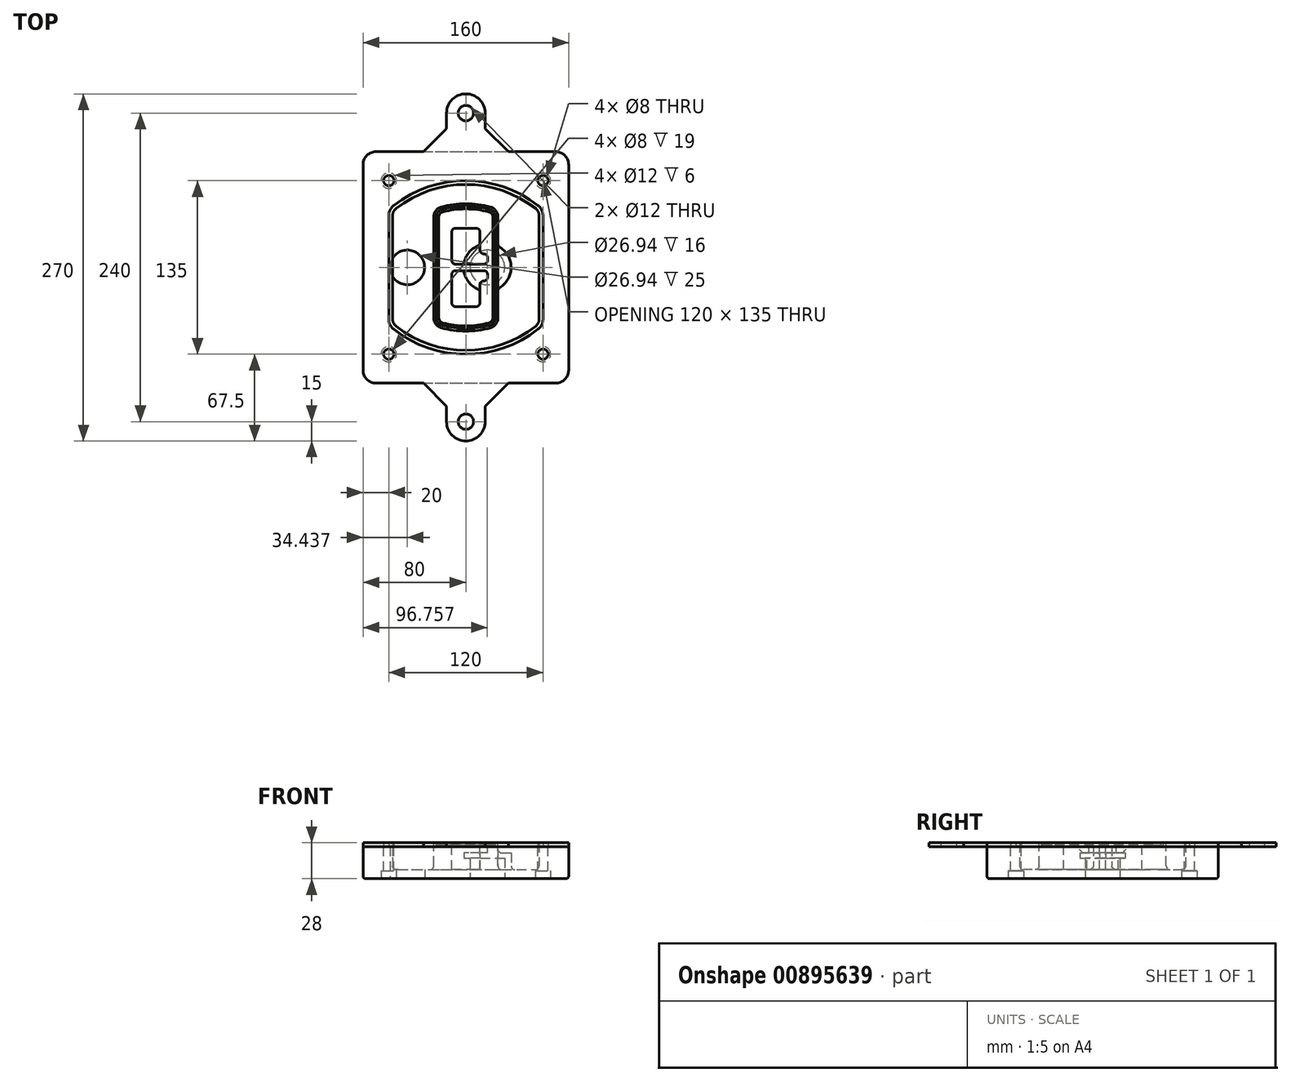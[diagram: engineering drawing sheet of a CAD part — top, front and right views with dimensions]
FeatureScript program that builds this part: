
annotation { "Feature Type Name" : "Feature", "Feature Type Description" : "" }
export const myFeature = defineFeature(function(context is Context, id is Id, definition is map)
    precondition{}
    {
        {
            var Q0;
            Q0=qCreatedBy(makeId("Top.planeOp"),FACE);
            var sketch = newSketch(context, id + "F0", { "sketchPlane" : qUnion([Q0])});
            skPoint(sketch, "E0.rect.middle", {"position": v(0, 0) * mm});
            skLineSegment(sketch, "E1.bottom", {"start": v(-70, -90) * mm, "end": v(70, -90) * mm});
            skLineSegment(sketch, "E1.top", {"start": v(-70, 90) * mm, "end": v(70, 90) * mm});
            skLineSegment(sketch, "E1.left", {"start": v(-80, -80) * mm, "end": v(-80, 80) * mm});
            skLineSegment(sketch, "E1.right", {"start": v(80, -80) * mm, "end": v(80, 80) * mm});
            skLineSegment(sketch, "E2", {"start": v(-80, 90) * mm, "end": v(80, -90) * mm, "construction": true});
            skLineSegment(sketch, "E3", {"start": v(80, 90) * mm, "end": v(-80, -90) * mm, "construction": true});
            skCircle(sketch, "E4", {"center": v(-60, 67.5) * mm, "radius": 4 * mm});
            skCircle(sketch, "E5", {"center": v(60, 67.5) * mm, "radius": 4 * mm});
            skCircle(sketch, "E6", {"center": v(60, -67.5) * mm, "radius": 4 * mm});
            skCircle(sketch, "E7", {"center": v(-60, -67.5) * mm, "radius": 4 * mm});
            skLineSegment(sketch, "E8", {"start": v(-60, 67.5) * mm, "end": v(60, 67.5) * mm, "construction": true});
            skLineSegment(sketch, "E9", {"start": v(60, 67.5) * mm, "end": v(60, -67.5) * mm, "construction": true});
            skLineSegment(sketch, "E10", {"start": v(60, -67.5) * mm, "end": v(-60, -67.5) * mm, "construction": true});
            skLineSegment(sketch, "E11", {"start": v(-60, -67.5) * mm, "end": v(-60, 67.5) * mm, "construction": true});
            skLineSegment(sketch, "E12", {"start": v(-60, 40.3) * mm, "end": v(-60, -40.3) * mm});
            skLineSegment(sketch, "E13", {"start": v(60, 40.3) * mm, "end": v(60, -40.3) * mm});
            skArc(sketch, "E14", {"start": v(56.15, 48.18) * mm, "mid": v(0, 67.5) * mm, "end": v(-56.15, 48.18) * mm});
            skArc(sketch, "E15", {"start": v(-56.15, -48.18) * mm, "mid": v(0, -67.5) * mm, "end": v(56.15, -48.18) * mm});
            skLineSegment(sketch, "E16", {"start": v(-60, 0) * mm, "end": v(60, 0) * mm, "construction": true});
            skPoint(sketch, "E17.visualSharp", {"position": v(-60, -45) * mm});
            skArc(sketch, "E17.filletArc", {"start": v(-60, -40.3) * mm, "mid": v(-58.99, -44.68) * mm, "end": v(-56.15, -48.18) * mm});
            skPoint(sketch, "E18.visualSharp", {"position": v(-60, 45) * mm});
            skArc(sketch, "E18.filletArc", {"start": v(-56.15, 48.18) * mm, "mid": v(-58.99, 44.68) * mm, "end": v(-60, 40.3) * mm});
            skPoint(sketch, "E19.visualSharp", {"position": v(60, 45) * mm});
            skArc(sketch, "E19.filletArc", {"start": v(60, 40.3) * mm, "mid": v(58.99, 44.68) * mm, "end": v(56.15, 48.18) * mm});
            skPoint(sketch, "E20.visualSharp", {"position": v(60, -45) * mm});
            skArc(sketch, "E20.filletArc", {"start": v(56.15, -48.18) * mm, "mid": v(58.99, -44.68) * mm, "end": v(60, -40.3) * mm});
            skPoint(sketch, "E21.visualSharp", {"position": v(-80, 90) * mm});
            skArc(sketch, "E21.filletArc", {"start": v(-70, 90) * mm, "mid": v(-77.07, 87.07) * mm, "end": v(-80, 80) * mm});
            skPoint(sketch, "E22.visualSharp", {"position": v(80, 90) * mm});
            skArc(sketch, "E22.filletArc", {"start": v(80, 80) * mm, "mid": v(77.07, 87.07) * mm, "end": v(70, 90) * mm});
            skPoint(sketch, "E23.visualSharp", {"position": v(80, -90) * mm});
            skArc(sketch, "E23.filletArc", {"start": v(70, -90) * mm, "mid": v(77.07, -87.07) * mm, "end": v(80, -80) * mm});
            skPoint(sketch, "E24.visualSharp", {"position": v(-80, -90) * mm});
            skArc(sketch, "E24.filletArc", {"start": v(-80, -80) * mm, "mid": v(-77.07, -87.07) * mm, "end": v(-70, -90) * mm});
            skArc(sketch, "E25.0", {"start": v(57, 40.3) * mm, "mid": v(56.3, 43.36) * mm, "end": v(54.3, 45.81) * mm});
            skLineSegment(sketch, "E25.1", {"start": v(57, 40.3) * mm, "end": v(57, -40.3) * mm});
            skArc(sketch, "E25.2", {"start": v(54.3, -45.81) * mm, "mid": v(56.3, -43.36) * mm, "end": v(57, -40.3) * mm});
            skArc(sketch, "E25.3", {"start": v(-54.3, -45.81) * mm, "mid": v(0, -64.5) * mm, "end": v(54.3, -45.81) * mm});
            skArc(sketch, "E25.4", {"start": v(-57, -40.3) * mm, "mid": v(-56.3, -43.36) * mm, "end": v(-54.3, -45.81) * mm});
            skArc(sketch, "E25.5", {"start": v(54.3, 45.81) * mm, "mid": v(0, 64.5) * mm, "end": v(-54.3, 45.81) * mm});
            skLineSegment(sketch, "E25.6", {"start": v(-57, 40.3) * mm, "end": v(-57, -40.3) * mm});
            skArc(sketch, "E25.7", {"start": v(-54.3, 45.81) * mm, "mid": v(-56.3, 43.36) * mm, "end": v(-57, 40.3) * mm});
            skArc(sketch, "E26.0", {"start": v(-58.62, 51.33) * mm, "mid": v(-62.58, 46.43) * mm, "end": v(-64, 40.3) * mm});
            skArc(sketch, "E26.1", {"start": v(58.62, 51.33) * mm, "mid": v(0, 71.5) * mm, "end": v(-58.62, 51.33) * mm});
            skArc(sketch, "E26.2", {"start": v(64, 40.3) * mm, "mid": v(62.58, 46.43) * mm, "end": v(58.62, 51.33) * mm});
            skLineSegment(sketch, "E26.3", {"start": v(64, 40.3) * mm, "end": v(64, -40.3) * mm});
            skArc(sketch, "E26.4", {"start": v(58.62, -51.33) * mm, "mid": v(62.58, -46.43) * mm, "end": v(64, -40.3) * mm});
            skLineSegment(sketch, "E26.5", {"start": v(-64, 40.3) * mm, "end": v(-64, -40.3) * mm});
            skArc(sketch, "E26.6", {"start": v(-58.62, -51.33) * mm, "mid": v(0, -71.5) * mm, "end": v(58.62, -51.33) * mm});
            skArc(sketch, "E26.7", {"start": v(-64, -40.3) * mm, "mid": v(-62.58, -46.43) * mm, "end": v(-58.62, -51.33) * mm});
            skSolve(sketch);
        }
        {
            var Q0;
            Q0=makeQuery(id+"F0.imprint","IMPRINT",FACE,{"disambiguationData":[TD([[makeQuery(id+"F0.imprint","IMPRINT",EDGE,{"derivedFrom":sQuery(id+"F0.wireOp",EDGE,"E1.bottom")}),1.0]])]});
            var Q1;
            Q1=makeQuery(id+"F0.imprint","IMPRINT",FACE,{"disambiguationData":[TD([[makeQuery(id+"F0.imprint","IMPRINT",EDGE,{"derivedFrom":sQuery(id+"F0.wireOp",EDGE,"E12")}),1.0]])]});
            var Q2;
            Q2=makeQuery(id+"F0.imprint","IMPRINT",FACE,{"disambiguationData":[TD([[makeQuery(id+"F0.imprint","IMPRINT",EDGE,{"derivedFrom":sQuery(id+"F0.wireOp",EDGE,"E25.0")}),1.0]])]});
            var Q3;
            Q3=makeQuery(id+"F0.imprint","IMPRINT",FACE,{"disambiguationData":[TD([[makeQuery(id+"F0.imprint","IMPRINT",EDGE,{"derivedFrom":sQuery(id+"F0.wireOp",EDGE,"E12")}),-1.0]])]});
            extrude(context, id + "F1", {"entities" : qUnion([Q0, Q1, Q2, Q3]), "oppositeDirection" : true, "depth" : 25 * mm});
        }
        {
            var Q0;
            Q0=makeQuery(id+"F0.imprint","IMPRINT",FACE,{"disambiguationData":[TD([[makeQuery(id+"F0.imprint","IMPRINT",EDGE,{"derivedFrom":sQuery(id+"F0.wireOp",EDGE,"E12")}),1.0]])]});
            extrude(context, id + "F2", {"entities" : qUnion([Q0]), "operationType" : NewBodyOperationType.ADD, "depth" : 3 * mm});
        }
        {
            var Q0;
            Q0=makeQuery(id+"F0.imprint","IMPRINT",FACE,{"disambiguationData":[TD([[makeQuery(id+"F0.imprint","IMPRINT",EDGE,{"derivedFrom":sQuery(id+"F0.wireOp",EDGE,"E25.0")}),1.0]])]});
            extrude(context, id + "F3", {"entities" : qUnion([Q0]), "operationType" : NewBodyOperationType.REMOVE, "oppositeDirection" : true, "depth" : 18 * mm});
        }
        {
            var Q0;
            Q0=makeQuery(id+"F2.opExtrude","CAP_FACE",FACE,{"disambiguationData":[OSD([sQuery(id+"F0.wireOp",EDGE,"E12"),sQuery(id+"F0.wireOp",EDGE,"E13"),sQuery(id+"F0.wireOp",EDGE,"E14"),sQuery(id+"F0.wireOp",EDGE,"E15"),sQuery(id+"F0.wireOp",EDGE,"E17.filletArc"),sQuery(id+"F0.wireOp",EDGE,"E18.filletArc"),sQuery(id+"F0.wireOp",EDGE,"E19.filletArc"),sQuery(id+"F0.wireOp",EDGE,"E20.filletArc"),sQuery(id+"F0.wireOp",EDGE,"E25.0"),sQuery(id+"F0.wireOp",EDGE,"E25.1"),sQuery(id+"F0.wireOp",EDGE,"E25.2"),sQuery(id+"F0.wireOp",EDGE,"E25.3"),sQuery(id+"F0.wireOp",EDGE,"E25.4"),sQuery(id+"F0.wireOp",EDGE,"E25.5"),sQuery(id+"F0.wireOp",EDGE,"E25.6"),sQuery(id+"F0.wireOp",EDGE,"E25.7")])],"isStart":false});
            var sketch = newSketch(context, id + "F4", { "sketchPlane" : qUnion([Q0])});
            skArc(sketch, "E27.0", {"start": v(-19.08, -46.97) * mm, "mid": v(0, -49.5) * mm, "end": v(19.08, -46.97) * mm});
            skArc(sketch, "E28.0", {"start": v(19.08, 46.97) * mm, "mid": v(0, 49.5) * mm, "end": v(-19.08, 46.97) * mm});
            skLineSegment(sketch, "E29", {"start": v(-25, 39.25) * mm, "end": v(-25, -39.25) * mm});
            skLineSegment(sketch, "E30", {"start": v(25, 39.25) * mm, "end": v(25, -39.25) * mm});
            skLineSegment(sketch, "E31", {"start": v(-25, 45.1) * mm, "end": v(25, 45.1) * mm, "construction": true});
            skLineSegment(sketch, "E32", {"start": v(-25, -45.1) * mm, "end": v(25, -45.1) * mm, "construction": true});
            skPoint(sketch, "E33.visualSharp", {"position": v(-25, 45.1) * mm});
            skArc(sketch, "E33.filletArc", {"start": v(-19.08, 46.97) * mm, "mid": v(-23.35, 44.11) * mm, "end": v(-25, 39.25) * mm});
            skPoint(sketch, "E34.visualSharp", {"position": v(25, 45.1) * mm});
            skArc(sketch, "E34.filletArc", {"start": v(25, 39.25) * mm, "mid": v(23.35, 44.11) * mm, "end": v(19.08, 46.97) * mm});
            skPoint(sketch, "E35.visualSharp", {"position": v(25, -45.1) * mm});
            skArc(sketch, "E35.filletArc", {"start": v(19.08, -46.97) * mm, "mid": v(23.35, -44.11) * mm, "end": v(25, -39.25) * mm});
            skPoint(sketch, "E36.visualSharp", {"position": v(-25, -45.1) * mm});
            skArc(sketch, "E36.filletArc", {"start": v(-25, -39.25) * mm, "mid": v(-23.35, -44.11) * mm, "end": v(-19.08, -46.97) * mm});
            skArc(sketch, "E37.0", {"start": v(54.3, 45.81) * mm, "mid": v(0, 64.5) * mm, "end": v(-54.3, 45.81) * mm});
            skArc(sketch, "E37.1", {"start": v(-54.3, 45.81) * mm, "mid": v(-56.3, 43.36) * mm, "end": v(-57, 40.3) * mm});
            skLineSegment(sketch, "E37.2", {"start": v(-57, 40.3) * mm, "end": v(-57, -40.3) * mm});
            skArc(sketch, "E37.3", {"start": v(-57, -40.3) * mm, "mid": v(-56.3, -43.36) * mm, "end": v(-54.3, -45.81) * mm});
            skArc(sketch, "E37.4", {"start": v(-54.3, -45.81) * mm, "mid": v(0, -64.5) * mm, "end": v(54.3, -45.81) * mm});
            skArc(sketch, "E37.5", {"start": v(54.3, -45.81) * mm, "mid": v(56.3, -43.36) * mm, "end": v(57, -40.3) * mm});
            skLineSegment(sketch, "E37.6", {"start": v(57, 40.3) * mm, "end": v(57, -40.3) * mm});
            skArc(sketch, "E37.7", {"start": v(57, 40.3) * mm, "mid": v(56.3, 43.36) * mm, "end": v(54.3, 45.81) * mm});
            skLineSegment(sketch, "E38.0", {"start": v(23, 39.25) * mm, "end": v(23, -39.25) * mm});
            skArc(sketch, "E38.1", {"start": v(18.56, -45.04) * mm, "mid": v(21.76, -42.9) * mm, "end": v(23, -39.25) * mm});
            skArc(sketch, "E38.2", {"start": v(-18.56, -45.04) * mm, "mid": v(0, -47.5) * mm, "end": v(18.56, -45.04) * mm});
            skArc(sketch, "E38.3", {"start": v(-23, -39.25) * mm, "mid": v(-21.76, -42.9) * mm, "end": v(-18.56, -45.04) * mm});
            skLineSegment(sketch, "E38.4", {"start": v(-23, 39.25) * mm, "end": v(-23, -39.25) * mm});
            skArc(sketch, "E38.5", {"start": v(23, 39.25) * mm, "mid": v(21.76, 42.9) * mm, "end": v(18.56, 45.04) * mm});
            skArc(sketch, "E38.6", {"start": v(-18.56, 45.04) * mm, "mid": v(-21.76, 42.9) * mm, "end": v(-23, 39.25) * mm});
            skArc(sketch, "E38.7", {"start": v(18.56, 45.04) * mm, "mid": v(0, 47.5) * mm, "end": v(-18.56, 45.04) * mm});
            skArc(sketch, "E39.0", {"start": v(21, 39.25) * mm, "mid": v(20.18, 41.68) * mm, "end": v(18.04, 43.1) * mm});
            skLineSegment(sketch, "E39.1", {"start": v(21, 39.25) * mm, "end": v(21, -39.25) * mm});
            skArc(sketch, "E39.2", {"start": v(18.04, -43.1) * mm, "mid": v(20.18, -41.68) * mm, "end": v(21, -39.25) * mm});
            skArc(sketch, "E39.3", {"start": v(-18.04, -43.1) * mm, "mid": v(0, -45.5) * mm, "end": v(18.04, -43.1) * mm});
            skArc(sketch, "E39.4", {"start": v(-21, -39.25) * mm, "mid": v(-20.18, -41.68) * mm, "end": v(-18.04, -43.1) * mm});
            skArc(sketch, "E39.5", {"start": v(18.04, 43.1) * mm, "mid": v(0, 45.5) * mm, "end": v(-18.04, 43.1) * mm});
            skLineSegment(sketch, "E39.6", {"start": v(-21, 39.25) * mm, "end": v(-21, -39.25) * mm});
            skArc(sketch, "E39.7", {"start": v(-18.04, 43.1) * mm, "mid": v(-20.18, 41.68) * mm, "end": v(-21, 39.25) * mm});
            skLineSegment(sketch, "E40", {"start": v(-25, 0) * mm, "end": v(25, 0) * mm, "construction": true});
            skLineSegment(sketch, "E41", {"start": v(-11, 5.5) * mm, "end": v(-11, 27.5) * mm});
            skLineSegment(sketch, "E42", {"start": v(-8, 30.5) * mm, "end": v(8, 30.5) * mm});
            skLineSegment(sketch, "E43", {"start": v(11, 27.5) * mm, "end": v(11, 13.5) * mm});
            skLineSegment(sketch, "E44", {"start": v(14, 10.5) * mm, "end": v(14, 10.5) * mm});
            skLineSegment(sketch, "E45", {"start": v(17, 7.5) * mm, "end": v(17, 5.5) * mm});
            skLineSegment(sketch, "E46", {"start": v(14, 2.5) * mm, "end": v(-8, 2.5) * mm});
            skPoint(sketch, "E47.visualSharp", {"position": v(-11, 30.5) * mm});
            skArc(sketch, "E47.filletArc", {"start": v(-8, 30.5) * mm, "mid": v(-10.12, 29.62) * mm, "end": v(-11, 27.5) * mm});
            skPoint(sketch, "E48.visualSharp", {"position": v(11, 30.5) * mm});
            skArc(sketch, "E48.filletArc", {"start": v(11, 27.5) * mm, "mid": v(10.12, 29.62) * mm, "end": v(8, 30.5) * mm});
            skPoint(sketch, "E49.visualSharp", {"position": v(11, 10.5) * mm});
            skArc(sketch, "E49.filletArc", {"start": v(11, 13.5) * mm, "mid": v(11.88, 11.38) * mm, "end": v(14, 10.5) * mm});
            skPoint(sketch, "E50.visualSharp", {"position": v(17, 10.5) * mm});
            skArc(sketch, "E50.filletArc", {"start": v(17, 7.5) * mm, "mid": v(16.12, 9.62) * mm, "end": v(14, 10.5) * mm});
            skPoint(sketch, "E51.visualSharp", {"position": v(17, 2.5) * mm});
            skArc(sketch, "E51.filletArc", {"start": v(14, 2.5) * mm, "mid": v(16.12, 3.38) * mm, "end": v(17, 5.5) * mm});
            skPoint(sketch, "E52.visualSharp", {"position": v(-11, 2.5) * mm});
            skArc(sketch, "E52.filletArc", {"start": v(-11, 5.5) * mm, "mid": v(-10.12, 3.38) * mm, "end": v(-8, 2.5) * mm});
            skLineSegment(sketch, "E53.0.MirrorCS", {"start": v(14, -2.5) * mm, "end": v(-8, -2.5) * mm});
            skArc(sketch, "E54.0.MirrorCS", {"start": v(-11, -5.5) * mm, "mid": v(-10.12, -3.38) * mm, "end": v(-8, -2.5) * mm});
            skLineSegment(sketch, "E55.0.MirrorCS", {"start": v(-11, -5.5) * mm, "end": v(-11, -27.5) * mm});
            skArc(sketch, "E56.0.MirrorCS", {"start": v(-8, -30.5) * mm, "mid": v(-10.12, -29.62) * mm, "end": v(-11, -27.5) * mm});
            skLineSegment(sketch, "E57.0.MirrorCS", {"start": v(-8, -30.5) * mm, "end": v(8, -30.5) * mm});
            skArc(sketch, "E58.0.MirrorCS", {"start": v(11, -27.5) * mm, "mid": v(10.12, -29.62) * mm, "end": v(8, -30.5) * mm});
            skLineSegment(sketch, "E59.0.MirrorCS", {"start": v(11, -27.5) * mm, "end": v(11, -13.5) * mm});
            skArc(sketch, "E60.0.MirrorCS", {"start": v(11, -13.5) * mm, "mid": v(11.88, -11.38) * mm, "end": v(14, -10.5) * mm});
            skArc(sketch, "E61.0.MirrorCS", {"start": v(17, -7.5) * mm, "mid": v(16.12, -9.62) * mm, "end": v(14, -10.5) * mm});
            skLineSegment(sketch, "E62.0.MirrorCS", {"start": v(17, -7.5) * mm, "end": v(17, -5.5) * mm});
            skArc(sketch, "E63.0.MirrorCS", {"start": v(14, -2.5) * mm, "mid": v(16.12, -3.38) * mm, "end": v(17, -5.5) * mm});
            skSolve(sketch);
        }
        {
            var Q0;
            Q0=makeQuery(id+"F4.imprint","IMPRINT",FACE,{"disambiguationData":[TD([[makeQuery(id+"F4.imprint","IMPRINT",EDGE,{"derivedFrom":sQuery(id+"F4.wireOp",EDGE,"E27.0")}),1.0]])]});
            var Q1;
            Q1=makeQuery(id+"F4.imprint","IMPRINT",FACE,{"disambiguationData":[TD([[makeQuery(id+"F4.imprint","IMPRINT",EDGE,{"derivedFrom":sQuery(id+"F4.wireOp",EDGE,"E38.0")}),-1.0]])]});
            var Q2;
            Q2=makeQuery(id+"F4.imprint","IMPRINT",FACE,{"disambiguationData":[TD([[makeQuery(id+"F4.imprint","IMPRINT",EDGE,{"derivedFrom":sQuery(id+"F4.wireOp",EDGE,"E39.0")}),1.0]])]});
            extrude(context, id + "F5", {"entities" : qUnion([Q0, Q1, Q2]), "operationType" : NewBodyOperationType.ADD, "endBound" : BoundingType.UP_TO_NEXT, "oppositeDirection" : true, "depth" : 25 * mm});
        }
        {
            var Q0;
            Q0=makeQuery(id+"F4.imprint","IMPRINT",FACE,{"disambiguationData":[TD([[makeQuery(id+"F4.imprint","IMPRINT",EDGE,{"derivedFrom":sQuery(id+"F4.wireOp",EDGE,"E38.0")}),-1.0]])]});
            extrude(context, id + "F6", {"entities" : qUnion([Q0]), "operationType" : NewBodyOperationType.REMOVE, "oppositeDirection" : true, "depth" : 2 * mm});
        }
        {
            var Q0;
            Q0=makeQuery(id+"F1.opExtrude","CAP_FACE",FACE,{"disambiguationData":[OSD([sQuery(id+"F0.wireOp",EDGE,"E1.bottom"),sQuery(id+"F0.wireOp",EDGE,"E1.top"),sQuery(id+"F0.wireOp",EDGE,"E1.left"),sQuery(id+"F0.wireOp",EDGE,"E1.right"),sQuery(id+"F0.wireOp",EDGE,"E4"),sQuery(id+"F0.wireOp",EDGE,"E5"),sQuery(id+"F0.wireOp",EDGE,"E6"),sQuery(id+"F0.wireOp",EDGE,"E7"),sQuery(id+"F0.wireOp",EDGE,"E21.filletArc"),sQuery(id+"F0.wireOp",EDGE,"E22.filletArc"),sQuery(id+"F0.wireOp",EDGE,"E23.filletArc"),sQuery(id+"F0.wireOp",EDGE,"E24.filletArc")])],"isStart":false});
            var sketch = newSketch(context, id + "F7", { "sketchPlane" : qUnion([Q0])});
            skCircle(sketch, "E64", {"center": v(16.76, 0) * mm, "radius": 13.47 * mm});
            skCircle(sketch, "E65", {"center": v(-45.56, 0) * mm, "radius": 13.47 * mm});
            skLineSegment(sketch, "E66", {"start": v(80, 0) * mm, "end": v(-80, 0) * mm});
            skCircle(sketch, "E67", {"center": v(16.76, 0) * mm, "radius": 18.47 * mm});
            skCircle(sketch, "E68", {"center": v(60, -67.5) * mm, "radius": 6 * mm});
            skCircle(sketch, "E69", {"center": v(-60, -67.5) * mm, "radius": 6 * mm});
            skCircle(sketch, "E70", {"center": v(-60, 67.5) * mm, "radius": 6 * mm});
            skCircle(sketch, "E71", {"center": v(60, 67.5) * mm, "radius": 6 * mm});
            skSolve(sketch);
        }
        {
            var Q0;
            {var subQ1=sQuery(id+"F7.wireOp",EDGE,"E66");var subQ4=sQuery(id+"F7.wireOp",EDGE,"E64");var subQ6=makeQuery(id+"F7.imprint","INTERSECT",VERTEX,{"disambiguationData":[OD(0.0)],"derivedFrom":[subQ4,subQ1]});Q0=makeQuery(id+"F7.imprint","IMPRINT",FACE,{"disambiguationData":[TD([[makeQuery(id+"F7.imprint","IMPRINT",EDGE,{"disambiguationData":[TD([[subQ6,-1.0]])],"derivedFrom":subQ4}),-1.0]])]});}
            var Q1;
            {var subQ0=sQuery(id+"F7.wireOp",EDGE,"E66");var subQ1=sQuery(id+"F7.wireOp",EDGE,"E64");var subQ3=makeQuery(id+"F7.imprint","INTERSECT",VERTEX,{"disambiguationData":[OD(0.0)],"derivedFrom":[subQ1,subQ0]});Q1=makeQuery(id+"F7.imprint","IMPRINT",FACE,{"disambiguationData":[TD([[makeQuery(id+"F7.imprint","IMPRINT",EDGE,{"disambiguationData":[TD([[subQ3,-1.0]])],"derivedFrom":subQ1}),1.0]])]});}
            var Q2;
            {var subQ0=sQuery(id+"F7.wireOp",EDGE,"E66");var subQ1=sQuery(id+"F7.wireOp",EDGE,"E64");var subQ3=makeQuery(id+"F7.imprint","INTERSECT",VERTEX,{"disambiguationData":[OD(0.0)],"derivedFrom":[subQ1,subQ0]});Q2=makeQuery(id+"F7.imprint","IMPRINT",FACE,{"disambiguationData":[TD([[makeQuery(id+"F7.imprint","IMPRINT",EDGE,{"disambiguationData":[TD([[subQ3,1.0]])],"derivedFrom":subQ1}),1.0]])]});}
            var Q3;
            {var subQ1=sQuery(id+"F7.wireOp",EDGE,"E66");var subQ4=sQuery(id+"F7.wireOp",EDGE,"E64");var subQ6=makeQuery(id+"F7.imprint","INTERSECT",VERTEX,{"disambiguationData":[OD(0.0)],"derivedFrom":[subQ4,subQ1]});Q3=makeQuery(id+"F7.imprint","IMPRINT",FACE,{"disambiguationData":[TD([[makeQuery(id+"F7.imprint","IMPRINT",EDGE,{"disambiguationData":[TD([[subQ6,1.0]])],"derivedFrom":subQ4}),-1.0]])]});}
            extrude(context, id + "F8", {"entities" : qUnion([Q0, Q1, Q2, Q3]), "operationType" : NewBodyOperationType.ADD, "oppositeDirection" : true, "depth" : 20 * mm});
        }
        {
            var Q0;
            {var subQ0=sQuery(id+"F7.wireOp",EDGE,"E66");var subQ1=sQuery(id+"F7.wireOp",EDGE,"E64");var subQ3=makeQuery(id+"F7.imprint","INTERSECT",VERTEX,{"disambiguationData":[OD(0.0)],"derivedFrom":[subQ1,subQ0]});Q0=makeQuery(id+"F7.imprint","IMPRINT",FACE,{"disambiguationData":[TD([[makeQuery(id+"F7.imprint","IMPRINT",EDGE,{"disambiguationData":[TD([[subQ3,-1.0]])],"derivedFrom":subQ1}),1.0]])]});}
            var Q1;
            {var subQ0=sQuery(id+"F7.wireOp",EDGE,"E66");var subQ1=sQuery(id+"F7.wireOp",EDGE,"E64");var subQ3=makeQuery(id+"F7.imprint","INTERSECT",VERTEX,{"disambiguationData":[OD(0.0)],"derivedFrom":[subQ1,subQ0]});Q1=makeQuery(id+"F7.imprint","IMPRINT",FACE,{"disambiguationData":[TD([[makeQuery(id+"F7.imprint","IMPRINT",EDGE,{"disambiguationData":[TD([[subQ3,1.0]])],"derivedFrom":subQ1}),1.0]])]});}
            extrude(context, id + "F9", {"entities" : qUnion([Q0, Q1]), "operationType" : NewBodyOperationType.REMOVE, "oppositeDirection" : true, "depth" : 16 * mm});
        }
        {
            var Q0;
            {var subQ0=sQuery(id+"F7.wireOp",EDGE,"E66");var subQ1=sQuery(id+"F7.wireOp",EDGE,"E65");var subQ3=makeQuery(id+"F7.imprint","INTERSECT",VERTEX,{"disambiguationData":[OD(0.0)],"derivedFrom":[subQ1,subQ0]});Q0=makeQuery(id+"F7.imprint","IMPRINT",FACE,{"disambiguationData":[TD([[makeQuery(id+"F7.imprint","IMPRINT",EDGE,{"disambiguationData":[TD([[subQ3,-1.0]])],"derivedFrom":subQ1}),1.0]])]});}
            var Q1;
            {var subQ0=sQuery(id+"F7.wireOp",EDGE,"E66");var subQ1=sQuery(id+"F7.wireOp",EDGE,"E65");var subQ3=makeQuery(id+"F7.imprint","INTERSECT",VERTEX,{"disambiguationData":[OD(0.0)],"derivedFrom":[subQ1,subQ0]});Q1=makeQuery(id+"F7.imprint","IMPRINT",FACE,{"disambiguationData":[TD([[makeQuery(id+"F7.imprint","IMPRINT",EDGE,{"disambiguationData":[TD([[subQ3,1.0]])],"derivedFrom":subQ1}),1.0]])]});}
            extrude(context, id + "F10", {"entities" : qUnion([Q0, Q1]), "operationType" : NewBodyOperationType.REMOVE, "oppositeDirection" : true, "depth" : 25 * mm});
        }
        {
            var Q0;
            Q0=makeQuery(id+"F7.imprint","IMPRINT",FACE,{"disambiguationData":[TD([[makeQuery(id+"F7.imprint","IMPRINT",EDGE,{"derivedFrom":sQuery(id+"F7.wireOp",EDGE,"E68")}),1.0]])]});
            var Q1;
            Q1=makeQuery(id+"F7.imprint","IMPRINT",FACE,{"disambiguationData":[TD([[makeQuery(id+"F7.imprint","IMPRINT",EDGE,{"derivedFrom":makeQuery(id+"F1.opExtrude","CAP_EDGE",EDGE,{"disambiguationData":[OSD([sQuery(id+"F0.wireOp",EDGE,"E5")])],"isStart":false})}),-1.0]])]});
            var Q2;
            Q2=makeQuery(id+"F7.imprint","IMPRINT",FACE,{"disambiguationData":[TD([[makeQuery(id+"F7.imprint","IMPRINT",EDGE,{"derivedFrom":sQuery(id+"F7.wireOp",EDGE,"E69")}),1.0]])]});
            var Q3;
            Q3=makeQuery(id+"F7.imprint","IMPRINT",FACE,{"disambiguationData":[TD([[makeQuery(id+"F7.imprint","IMPRINT",EDGE,{"derivedFrom":makeQuery(id+"F1.opExtrude","CAP_EDGE",EDGE,{"disambiguationData":[OSD([sQuery(id+"F0.wireOp",EDGE,"E4")])],"isStart":false})}),-1.0]])]});
            var Q4;
            Q4=makeQuery(id+"F7.imprint","IMPRINT",FACE,{"disambiguationData":[TD([[makeQuery(id+"F7.imprint","IMPRINT",EDGE,{"derivedFrom":sQuery(id+"F7.wireOp",EDGE,"E70")}),1.0]])]});
            var Q5;
            Q5=makeQuery(id+"F7.imprint","IMPRINT",FACE,{"disambiguationData":[TD([[makeQuery(id+"F7.imprint","IMPRINT",EDGE,{"derivedFrom":makeQuery(id+"F1.opExtrude","CAP_EDGE",EDGE,{"disambiguationData":[OSD([sQuery(id+"F0.wireOp",EDGE,"E7")])],"isStart":false})}),-1.0]])]});
            var Q6;
            Q6=makeQuery(id+"F7.imprint","IMPRINT",FACE,{"disambiguationData":[TD([[makeQuery(id+"F7.imprint","IMPRINT",EDGE,{"derivedFrom":sQuery(id+"F7.wireOp",EDGE,"E71")}),1.0]])]});
            var Q7;
            Q7=makeQuery(id+"F7.imprint","IMPRINT",FACE,{"disambiguationData":[TD([[makeQuery(id+"F7.imprint","IMPRINT",EDGE,{"derivedFrom":makeQuery(id+"F1.opExtrude","CAP_EDGE",EDGE,{"disambiguationData":[OSD([sQuery(id+"F0.wireOp",EDGE,"E6")])],"isStart":false})}),-1.0]])]});
            extrude(context, id + "F11", {"entities" : qUnion([Q0, Q1, Q2, Q3, Q4, Q5, Q6, Q7]), "operationType" : NewBodyOperationType.REMOVE, "oppositeDirection" : true, "depth" : 6 * mm});
        }
        {
            var Q0;
            Q0=makeQuery(id+"F9.boolean.opBoolean","COPY",FACE,{"derivedFrom":makeQuery(id+"F9.opExtrude","CAP_FACE",FACE,{"disambiguationData":[OSD([sQuery(id+"F7.wireOp",EDGE,"E64")])],"isStart":false})});
            var sketch = newSketch(context, id + "F12", { "sketchPlane" : qUnion([Q0])});
            skArc(sketch, "E72.0", {"start": v(11, 17.55) * mm, "mid": v(2.57, 11.82) * mm, "end": v(-1.54, 2.5) * mm});
            skArc(sketch, "E72.1", {"start": v(-1.54, -2.5) * mm, "mid": v(2.57, -11.82) * mm, "end": v(11, -17.55) * mm});
            skLineSegment(sketch, "E73", {"start": v(-1.54, -2.5) * mm, "end": v(14, -2.5) * mm});
            skLineSegment(sketch, "E74.0", {"start": v(14, 2.5) * mm, "end": v(-1.54, 2.5) * mm});
            skArc(sketch, "E74.1", {"start": v(14, 2.5) * mm, "mid": v(16.12, 3.38) * mm, "end": v(17, 5.5) * mm});
            skLineSegment(sketch, "E74.2", {"start": v(17, 7.5) * mm, "end": v(17, 5.5) * mm});
            skArc(sketch, "E74.3", {"start": v(17, 7.5) * mm, "mid": v(16.12, 9.62) * mm, "end": v(14, 10.5) * mm});
            skArc(sketch, "E74.4", {"start": v(11, 13.5) * mm, "mid": v(11.88, 11.38) * mm, "end": v(14, 10.5) * mm});
            skLineSegment(sketch, "E74.5", {"start": v(11, 17.55) * mm, "end": v(11, 13.5) * mm});
            skLineSegment(sketch, "E74.7", {"start": v(14, -2.5) * mm, "end": v(-1.54, -2.5) * mm});
            skArc(sketch, "E74.8", {"start": v(14, -2.5) * mm, "mid": v(16.12, -3.38) * mm, "end": v(17, -5.5) * mm});
            skLineSegment(sketch, "E74.9", {"start": v(17, -7.5) * mm, "end": v(17, -5.5) * mm});
            skArc(sketch, "E74.10", {"start": v(17, -7.5) * mm, "mid": v(16.12, -9.62) * mm, "end": v(14, -10.5) * mm});
            skArc(sketch, "E74.11", {"start": v(11, -13.5) * mm, "mid": v(11.88, -11.38) * mm, "end": v(14, -10.5) * mm});
            skLineSegment(sketch, "E74.12", {"start": v(11, -17.55) * mm, "end": v(11, -13.5) * mm});
            skPoint(sketch, "E75.orphan", {"position": v(11, -27.5) * mm});
            skPoint(sketch, "E76.orphan", {"position": v(-8, -2.5) * mm});
            skPoint(sketch, "E77.orphan", {"position": v(-8, 2.5) * mm});
            skPoint(sketch, "E78.orphan", {"position": v(11, 27.5) * mm});
            skSolve(sketch);
        }
        {
            var Q0;
            {var subQ7=sQuery(id+"F12.wireOp",EDGE,"E72.0");var subQ14=sQuery(id+"F12.wireOp",EDGE,"E72.1");var subQ16=sQuery(id+"F12.wireOp",EDGE,"E74.1");var subQ18=sQuery(id+"F12.wireOp",EDGE,"E74.8");Q0=qUnion([makeQuery(id+"F12.imprint","IMPRINT",FACE,{"disambiguationData":[TD([[makeQuery(id+"F12.imprint","IMPRINT",EDGE,{"derivedFrom":subQ7}),1.0]])]}),makeQuery(id+"F12.imprint","IMPRINT",FACE,{"disambiguationData":[TD([[makeQuery(id+"F12.imprint","IMPRINT",EDGE,{"derivedFrom":subQ14}),1.0]])]}),makeQuery(id+"F12.imprint","IMPRINT",FACE,{"disambiguationData":[TD([[makeQuery(id+"F12.imprint","IMPRINT",EDGE,{"derivedFrom":subQ16}),1.0]])]}),makeQuery(id+"F12.imprint","IMPRINT",FACE,{"disambiguationData":[TD([[makeQuery(id+"F12.imprint","IMPRINT",EDGE,{"derivedFrom":subQ18}),-1.0]])]})]);}
            var Q1;
            Q1=makeQuery(id+"F5.boolean.opBoolean","SPLIT",FACE,{"disambiguationData":[TD([makeQuery(id+"F5.opExtrude","SWEPT_FACE",FACE,{"disambiguationData":[OSD([sQuery(id+"F4.wireOp",EDGE,"E41")])]})])],"derivedFrom":makeQuery(id+"F3.boolean.opBoolean","COPY",FACE,{"derivedFrom":makeQuery(id+"F3.opExtrude","CAP_FACE",FACE,{"disambiguationData":[OSD([sQuery(id+"F0.wireOp",EDGE,"E25.0"),sQuery(id+"F0.wireOp",EDGE,"E25.1"),sQuery(id+"F0.wireOp",EDGE,"E25.2"),sQuery(id+"F0.wireOp",EDGE,"E25.3"),sQuery(id+"F0.wireOp",EDGE,"E25.4"),sQuery(id+"F0.wireOp",EDGE,"E25.5"),sQuery(id+"F0.wireOp",EDGE,"E25.6"),sQuery(id+"F0.wireOp",EDGE,"E25.7")])],"isStart":false})})});
            extrude(context, id + "F13", {"entities" : qUnion([Q0]), "operationType" : NewBodyOperationType.REMOVE, "endBound" : BoundingType.UP_TO_SURFACE, "endBoundEntityFace" : qUnion([Q1]), "depth" : 25 * mm});
        }
        {
            var Q0;
            Q0=makeQuery(id+"F3.boolean.opBoolean","COPY",EDGE,{"derivedFrom":makeQuery(id+"F3.opExtrude","CAP_EDGE",EDGE,{"disambiguationData":[OSD([sQuery(id+"F0.wireOp",EDGE,"E25.6")])],"isStart":false})});
            var Q1;
            Q1=makeQuery(id+"F8.boolean.opBoolean","INTERSECT",EDGE,{"derivedFrom":[makeQuery(id+"F5.opExtrude","SWEPT_FACE",FACE,{"disambiguationData":[OSD([sQuery(id+"F4.wireOp",EDGE,"E30")])]}),makeQuery(id+"F8.opExtrude","CAP_FACE",FACE,{"disambiguationData":[OSD([sQuery(id+"F7.wireOp",EDGE,"E67")])],"isStart":false})]});
            var Q2;
            Q2=makeQuery(id+"F8.boolean.opBoolean","INTERSECT",EDGE,{"disambiguationData":[OD(1.0)],"derivedFrom":[makeQuery(id+"F5.opExtrude","SWEPT_FACE",FACE,{"disambiguationData":[OSD([sQuery(id+"F4.wireOp",EDGE,"E30")])]}),makeQuery(id+"F8.opExtrude","SWEPT_FACE",FACE,{"disambiguationData":[OSD([sQuery(id+"F7.wireOp",EDGE,"E67")])]})]});
            var Q3;
            {var subQ0=sQuery(id+"F4.wireOp",EDGE,"E30");Q3=makeQuery(id+"F8.boolean.opBoolean","SPLIT",EDGE,{"disambiguationData":[TD([makeQuery(id+"F5.opExtrude","SWEPT_FACE",FACE,{"disambiguationData":[OSD([sQuery(id+"F4.wireOp",EDGE,"E35.filletArc")])]})])],"derivedFrom":makeQuery(id+"F5.opExtrude","CAP_EDGE",EDGE,{"disambiguationData":[OSD([subQ0])],"isStart":false})});}
            var Q4;
            {var subQ0=sQuery(id+"F0.wireOp",EDGE,"E25.7");var subQ1=sQuery(id+"F0.wireOp",EDGE,"E25.1");var subQ2=sQuery(id+"F0.wireOp",EDGE,"E25.6");var subQ3=sQuery(id+"F0.wireOp",EDGE,"E25.5");var subQ4=sQuery(id+"F0.wireOp",EDGE,"E25.4");var subQ5=sQuery(id+"F0.wireOp",EDGE,"E25.0");var subQ6=sQuery(id+"F0.wireOp",EDGE,"E25.2");var subQ7=sQuery(id+"F0.wireOp",EDGE,"E25.3");Q4=makeQuery(id+"F8.boolean.opBoolean","INTERSECT",EDGE,{"derivedFrom":[makeQuery(id+"F5.boolean.opBoolean","SPLIT",FACE,{"disambiguationData":[TD([makeQuery(id+"F2.opExtrude","SWEPT_FACE",FACE,{"disambiguationData":[OSD([subQ5])]})])],"derivedFrom":makeQuery(id+"F3.boolean.opBoolean","COPY",FACE,{"derivedFrom":makeQuery(id+"F3.opExtrude","CAP_FACE",FACE,{"disambiguationData":[OSD([subQ5,subQ1,subQ6,subQ7,subQ4,subQ3,subQ2,subQ0])],"isStart":false})})}),makeQuery(id+"F8.opExtrude","SWEPT_FACE",FACE,{"disambiguationData":[OSD([sQuery(id+"F7.wireOp",EDGE,"E67")])]})]});}
            var Q5;
            Q5=makeQuery(id+"F8.boolean.opBoolean","INTERSECT",EDGE,{"disambiguationData":[OD(0.0)],"derivedFrom":[makeQuery(id+"F5.opExtrude","SWEPT_FACE",FACE,{"disambiguationData":[OSD([sQuery(id+"F4.wireOp",EDGE,"E30")])]}),makeQuery(id+"F8.opExtrude","SWEPT_FACE",FACE,{"disambiguationData":[OSD([sQuery(id+"F7.wireOp",EDGE,"E67")])]})]});
            fillet(context, id + "F14", {"entities" : qUnion([Q0, Q1, Q2, Q3, Q4, Q5]), "radius" : 3 * mm, "tangentPropagation" : true, "allowEdgeOverflow" : false});
        }
        {
            var Q0;
            Q0=makeQuery(id+"F1.opExtrude","CAP_EDGE",EDGE,{"disambiguationData":[OSD([sQuery(id+"F0.wireOp",EDGE,"E1.bottom")])],"isStart":false});
            fillet(context, id + "F15", {"entities" : qUnion([Q0]), "radius" : 2 * mm, "tangentPropagation" : true, "allowEdgeOverflow" : false});
        }
        {
            var Q0;
            {var subQ0=sQuery(id+"F0.wireOp",EDGE,"E21.filletArc");var subQ1=sQuery(id+"F0.wireOp",EDGE,"E7");var subQ2=sQuery(id+"F0.wireOp",EDGE,"E6");var subQ3=sQuery(id+"F0.wireOp",EDGE,"E5");var subQ4=sQuery(id+"F0.wireOp",EDGE,"E4");var subQ5=sQuery(id+"F0.wireOp",EDGE,"E22.filletArc");var subQ6=sQuery(id+"F0.wireOp",EDGE,"E1.bottom");var subQ7=sQuery(id+"F0.wireOp",EDGE,"E1.right");var subQ8=sQuery(id+"F0.wireOp",EDGE,"E1.top");var subQ9=sQuery(id+"F0.wireOp",EDGE,"E1.left");var subQ10=sQuery(id+"F0.wireOp",EDGE,"E23.filletArc");var subQ11=sQuery(id+"F0.wireOp",EDGE,"E24.filletArc");Q0=makeQuery(id+"F2.boolean.opBoolean","SPLIT",FACE,{"disambiguationData":[TD([makeQuery(id+"F1.opExtrude","SWEPT_FACE",FACE,{"disambiguationData":[OSD([subQ6])]})])],"derivedFrom":makeQuery(id+"F1.opExtrude","CAP_FACE",FACE,{"disambiguationData":[OSD([subQ6,subQ8,subQ9,subQ7,subQ4,subQ3,subQ2,subQ1,subQ0,subQ5,subQ10,subQ11])],"isStart":true})});}
            var sketch = newSketch(context, id + "F16", { "sketchPlane" : qUnion([Q0])});
            skLineSegment(sketch, "E79", {"start": v(0, 120) * mm, "end": v(0, -160.81) * mm, "construction": true});
            skPoint(sketch, "E79.endSnap0", {"position": v(0, -90) * mm});
            skLineSegment(sketch, "E80", {"start": v(-120.68, 0) * mm, "end": v(137.03, 0) * mm, "construction": true});
            skLineSegment(sketch, "E81", {"start": v(-33, 90) * mm, "end": v(-15, 108) * mm});
            skLineSegment(sketch, "E82", {"start": v(33, 90) * mm, "end": v(15, 108) * mm});
            skLineSegment(sketch, "E83", {"start": v(-15, 108) * mm, "end": v(-15, 120) * mm});
            skLineSegment(sketch, "E84", {"start": v(15, 120) * mm, "end": v(15, 108) * mm});
            skArc(sketch, "E85", {"start": v(15, 120) * mm, "mid": v(0, 135) * mm, "end": v(-15, 120) * mm});
            skCircle(sketch, "E86", {"center": v(0, 120) * mm, "radius": 6 * mm});
            skLineSegment(sketch, "E87.MirrorCS", {"start": v(-33, -90) * mm, "end": v(-15, -108) * mm});
            skLineSegment(sketch, "E88.MirrorCS", {"start": v(33, -90) * mm, "end": v(15, -108) * mm});
            skLineSegment(sketch, "E89.MirrorCS", {"start": v(-15, -108) * mm, "end": v(-15, -120) * mm});
            skArc(sketch, "E90.MirrorCS", {"start": v(15, -120) * mm, "mid": v(0, -135) * mm, "end": v(-15, -120) * mm});
            skLineSegment(sketch, "E91.MirrorCS", {"start": v(15, -120) * mm, "end": v(15, -108) * mm});
            skCircle(sketch, "E92.MirrorC", {"center": v(0, -120) * mm, "radius": 6 * mm});
            skSolve(sketch);
        }
        {
            var Q0;
            {var subQ1=sQuery(id+"F16.wireOp",EDGE,"E87.MirrorCS");Q0=makeQuery(id+"F16.imprint","IMPRINT",FACE,{"disambiguationData":[TD([[makeQuery(id+"F16.imprint","IMPRINT",EDGE,{"derivedFrom":subQ1}),1.0]])]});}
            var Q1;
            Q1=makeQuery(id+"F16.imprint","IMPRINT",FACE,{"disambiguationData":[TD([[makeQuery(id+"F16.imprint","IMPRINT",EDGE,{"derivedFrom":makeQuery(id+"F1.opExtrude","CAP_EDGE",EDGE,{"disambiguationData":[OSD([sQuery(id+"F0.wireOp",EDGE,"E1.left")])],"isStart":true})}),-1.0]])]});
            var Q2;
            {var subQ0=sQuery(id+"F16.wireOp",EDGE,"E81");Q2=makeQuery(id+"F16.imprint","IMPRINT",FACE,{"disambiguationData":[TD([[makeQuery(id+"F16.imprint","IMPRINT",EDGE,{"derivedFrom":subQ0}),-1.0]])]});}
            var Q3;
            Q3=makeQuery(id+"F2.opExtrude","CAP_FACE",FACE,{"disambiguationData":[OSD([sQuery(id+"F0.wireOp",EDGE,"E12"),sQuery(id+"F0.wireOp",EDGE,"E13"),sQuery(id+"F0.wireOp",EDGE,"E14"),sQuery(id+"F0.wireOp",EDGE,"E15"),sQuery(id+"F0.wireOp",EDGE,"E17.filletArc"),sQuery(id+"F0.wireOp",EDGE,"E18.filletArc"),sQuery(id+"F0.wireOp",EDGE,"E19.filletArc"),sQuery(id+"F0.wireOp",EDGE,"E20.filletArc"),sQuery(id+"F0.wireOp",EDGE,"E25.0"),sQuery(id+"F0.wireOp",EDGE,"E25.1"),sQuery(id+"F0.wireOp",EDGE,"E25.2"),sQuery(id+"F0.wireOp",EDGE,"E25.3"),sQuery(id+"F0.wireOp",EDGE,"E25.4"),sQuery(id+"F0.wireOp",EDGE,"E25.5"),sQuery(id+"F0.wireOp",EDGE,"E25.6"),sQuery(id+"F0.wireOp",EDGE,"E25.7")])],"isStart":false});
            extrude(context, id + "F17", {"entities" : qUnion([Q0, Q1, Q2]), "endBound" : BoundingType.UP_TO_SURFACE, "depth" : 25 * mm, "endBoundEntityFace" : qUnion([Q3]), "offsetDistance" : 25 * mm});
        }
    });
